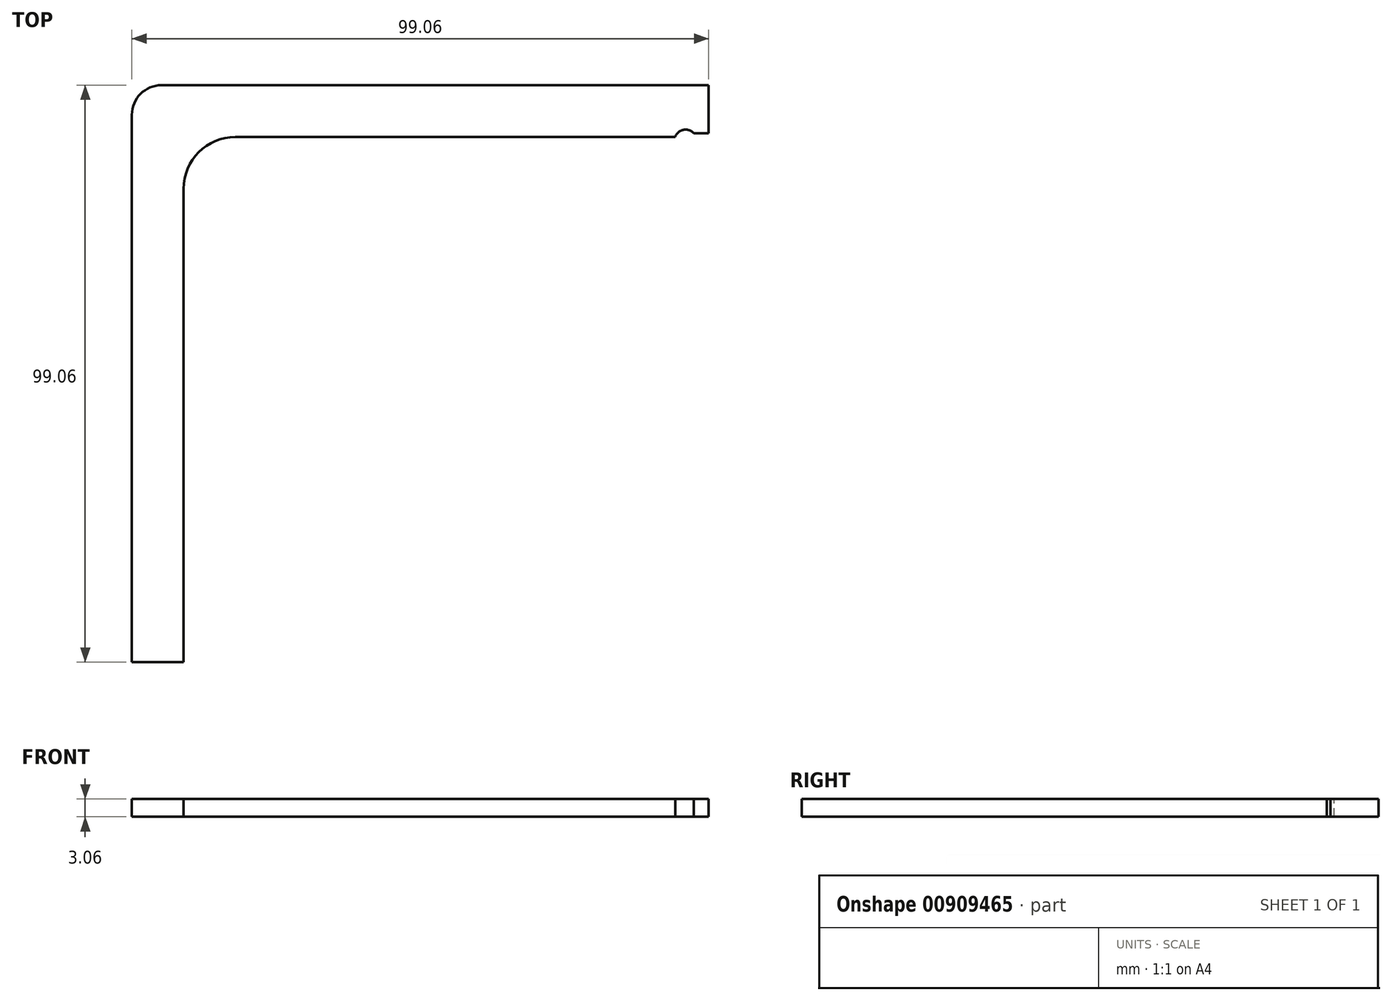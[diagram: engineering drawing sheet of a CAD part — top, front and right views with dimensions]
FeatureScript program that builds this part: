
annotation { "Feature Type Name" : "Feature", "Feature Type Description" : "" }
export const myFeature = defineFeature(function(context is Context, id is Id, definition is map)
    precondition{}
    {
        {
            var Q0;
            Q0=qCreatedBy(makeId("Top.planeOp"),FACE);
            var sketch = newSketch(context, id + "F0", { "sketchPlane" : qUnion([Q0])});
            skLineSegment(sketch, "E0.bottom", {"start": v(99.06, -99.06) * mm, "end": v(-99.06, -99.06) * mm});
            skLineSegment(sketch, "E0.top", {"start": v(99.06, 99.06) * mm, "end": v(-99.06, 99.06) * mm});
            skLineSegment(sketch, "E0.left", {"start": v(99.06, -99.06) * mm, "end": v(99.06, 99.06) * mm});
            skLineSegment(sketch, "E0.right", {"start": v(-99.06, -99.06) * mm, "end": v(-99.06, 99.06) * mm});
            skPoint(sketch, "E0.middle", {"position": v(0, 0) * mm});
            skLineSegment(sketch, "E1.bottom", {"start": v(86.36, 86.36) * mm, "end": v(-86.36, 86.36) * mm});
            skLineSegment(sketch, "E1.top", {"start": v(86.36, -86.36) * mm, "end": v(-86.36, -86.36) * mm});
            skLineSegment(sketch, "E1.left", {"start": v(86.36, 86.36) * mm, "end": v(86.36, -86.36) * mm});
            skLineSegment(sketch, "E1.right", {"start": v(-86.36, 86.36) * mm, "end": v(-86.36, -86.36) * mm});
            skSolve(sketch);
        }
        {
            var Q0;
            Q0=qSketchRegion(id+"F0",true);
            extrude(context, id + "F1", {"entities" : qUnion([Q0]), "depth" : (0.12 + 0.25 + (5.38 / 2)) * mm, "offsetDistance" : 25.4 * mm});
        }
        {
            var Q0;
            Q0=qCreatedBy(makeId("Top.planeOp"),FACE);
            cPlane(context, id + "F2", {"entities" : qUnion([Q0]), "cplaneType" : CPlaneType.OFFSET, "offset" : 6.35 * mm, "width" : 152.4 * mm, "height" : 152.4 * mm});
        }
        {
            var Q0;
            Q0=qCreatedBy(id+"F2.planeOp",FACE);
            var sketch = newSketch(context, id + "F3", { "sketchPlane" : qUnion([Q0])});
            skLineSegment(sketch, "E2.bottom", {"start": v(99.06, 99.06) * mm, "end": v(-99.06, 99.06) * mm});
            skLineSegment(sketch, "E2.top", {"start": v(99.06, -99.06) * mm, "end": v(-99.06, -99.06) * mm});
            skLineSegment(sketch, "E2.left", {"start": v(99.06, 99.06) * mm, "end": v(99.06, -99.06) * mm});
            skLineSegment(sketch, "E2.right", {"start": v(-99.06, 99.06) * mm, "end": v(-99.06, -99.06) * mm});
            skPoint(sketch, "E2.middle", {"position": v(0, 0) * mm});
            skLineSegment(sketch, "E3.bottom", {"start": v(92.71, 92.71) * mm, "end": v(-92.71, 92.71) * mm});
            skLineSegment(sketch, "E3.top", {"start": v(92.71, -92.71) * mm, "end": v(-92.71, -92.71) * mm});
            skLineSegment(sketch, "E3.left", {"start": v(92.71, 92.71) * mm, "end": v(92.71, -92.71) * mm});
            skLineSegment(sketch, "E3.right", {"start": v(-92.71, 92.71) * mm, "end": v(-92.71, -92.71) * mm});
            skSolve(sketch);
        }
        {
            var Q0;
            Q0=qSketchRegion(id+"F3",true);
            extrude(context, id + "F4", {"entities" : qUnion([Q0]), "operationType" : NewBodyOperationType.REMOVE, "endBound" : BoundingType.THROUGH_ALL, "depth" : 25.4 * mm, "offsetDistance" : 25.4 * mm});
        }
        {
            var Q0;
            Q0=makeQuery(id+"F1.opExtrude","SWEPT_EDGE",EDGE,{"disambiguationData":[OSD([sQuery(id+"F0.wireOp",EDGE,"E0.top"),sQuery(id+"F0.wireOp",EDGE,"E0.left")])]});
            var Q1;
            Q1=makeQuery(id+"F1.opExtrude","SWEPT_EDGE",EDGE,{"disambiguationData":[OSD([sQuery(id+"F0.wireOp",EDGE,"E0.top"),sQuery(id+"F0.wireOp",EDGE,"E0.right")])]});
            var Q2;
            Q2=makeQuery(id+"F4.boolean.opBoolean","COPY",EDGE,{"derivedFrom":makeQuery(id+"F4.opExtrude","SWEPT_EDGE",EDGE,{"disambiguationData":[OSD([sQuery(id+"F3.wireOp",EDGE,"E3.bottom"),sQuery(id+"F3.wireOp",EDGE,"E3.right")])]})});
            var Q3;
            Q3=makeQuery(id+"F4.boolean.opBoolean","COPY",EDGE,{"derivedFrom":makeQuery(id+"F4.opExtrude","SWEPT_EDGE",EDGE,{"disambiguationData":[OSD([sQuery(id+"F3.wireOp",EDGE,"E3.bottom"),sQuery(id+"F3.wireOp",EDGE,"E3.left")])]})});
            var Q4;
            Q4=makeQuery(id+"F1.opExtrude","SWEPT_EDGE",EDGE,{"disambiguationData":[OSD([sQuery(id+"F0.wireOp",EDGE,"E0.bottom"),sQuery(id+"F0.wireOp",EDGE,"E0.right")])]});
            var Q5;
            Q5=makeQuery(id+"F4.boolean.opBoolean","COPY",EDGE,{"derivedFrom":makeQuery(id+"F4.opExtrude","SWEPT_EDGE",EDGE,{"disambiguationData":[OSD([sQuery(id+"F3.wireOp",EDGE,"E3.top"),sQuery(id+"F3.wireOp",EDGE,"E3.right")])]})});
            var Q6;
            Q6=makeQuery(id+"F1.opExtrude","SWEPT_EDGE",EDGE,{"disambiguationData":[OSD([sQuery(id+"F0.wireOp",EDGE,"E0.bottom"),sQuery(id+"F0.wireOp",EDGE,"E0.left")])]});
            var Q7;
            Q7=makeQuery(id+"F4.boolean.opBoolean","COPY",EDGE,{"derivedFrom":makeQuery(id+"F4.opExtrude","SWEPT_EDGE",EDGE,{"disambiguationData":[OSD([sQuery(id+"F3.wireOp",EDGE,"E3.top"),sQuery(id+"F3.wireOp",EDGE,"E3.left")])]})});
            var Q8;
            Q8=makeQuery(id+"F1.opExtrude","SWEPT_EDGE",EDGE,{"disambiguationData":[OSD([sQuery(id+"F0.wireOp",EDGE,"E1.top"),sQuery(id+"F0.wireOp",EDGE,"E1.right")])]});
            var Q9;
            Q9=makeQuery(id+"F1.opExtrude","SWEPT_EDGE",EDGE,{"disambiguationData":[OSD([sQuery(id+"F0.wireOp",EDGE,"E1.top"),sQuery(id+"F0.wireOp",EDGE,"E1.left")])]});
            var Q10;
            Q10=makeQuery(id+"F1.opExtrude","SWEPT_EDGE",EDGE,{"disambiguationData":[OSD([sQuery(id+"F0.wireOp",EDGE,"E1.bottom"),sQuery(id+"F0.wireOp",EDGE,"E1.right")])]});
            var Q11;
            Q11=makeQuery(id+"F1.opExtrude","SWEPT_EDGE",EDGE,{"disambiguationData":[OSD([sQuery(id+"F0.wireOp",EDGE,"E1.bottom"),sQuery(id+"F0.wireOp",EDGE,"E1.left")])]});
            fillet(context, id + "F5", {"entities" : qUnion([Q0, Q1, Q2, Q3, Q4, Q5, Q6, Q7, Q8, Q9, Q10, Q11]), "radius" : 5.08 * mm, "tangentPropagation" : true, "allowEdgeOverflow" : false});
        }
        {
            var Q0;
            Q0=qCreatedBy(makeId("Front.planeOp"),FACE);
            var sketch = newSketch(context, id + "F6", { "sketchPlane" : qUnion([Q0])});
            skLineSegment(sketch, "E4.bottom", {"start": v(-137.33, -39.02) * mm, "end": v(163.38, -39.02) * mm});
            skLineSegment(sketch, "E4.top", {"start": v(-137.33, 123.29) * mm, "end": v(163.38, 123.29) * mm});
            skLineSegment(sketch, "E4.left", {"start": v(-137.33, -39.02) * mm, "end": v(-137.33, 123.29) * mm});
            skLineSegment(sketch, "E4.right", {"start": v(163.38, -39.02) * mm, "end": v(163.38, 123.29) * mm});
            skSolve(sketch);
        }
        {
            var Q0;
            Q0=qSketchRegion(id+"F6",true);
            extrude(context, id + "F7", {"entities" : qUnion([Q0]), "operationType" : NewBodyOperationType.REMOVE, "endBound" : BoundingType.THROUGH_ALL, "depth" : 25.4 * mm, "offsetDistance" : 25.4 * mm});
        }
        {
            var Q0;
            Q0=qCreatedBy(makeId("Right.planeOp"),FACE);
            var sketch = newSketch(context, id + "F8", { "sketchPlane" : qUnion([Q0])});
            skLineSegment(sketch, "E5.bottom", {"start": v(-40.9, -45.65) * mm, "end": v(117.43, -45.65) * mm});
            skLineSegment(sketch, "E5.top", {"start": v(-40.9, 78.34) * mm, "end": v(117.43, 78.34) * mm});
            skLineSegment(sketch, "E5.left", {"start": v(-40.9, -45.65) * mm, "end": v(-40.9, 78.34) * mm});
            skLineSegment(sketch, "E5.right", {"start": v(117.43, -45.65) * mm, "end": v(117.43, 78.34) * mm});
            skSolve(sketch);
        }
        {
            var Q0;
            Q0=qSketchRegion(id+"F8",true);
            extrude(context, id + "F9", {"entities" : qUnion([Q0]), "operationType" : NewBodyOperationType.REMOVE, "endBound" : BoundingType.THROUGH_ALL, "depth" : 25.4 * mm, "offsetDistance" : 25.4 * mm});
        }
        {
            var Q0;
            Q0=makeQuery(id+"F1.opExtrude","CAP_FACE",FACE,{"disambiguationData":[OSD([sQuery(id+"F0.wireOp",EDGE,"E0.bottom"),sQuery(id+"F0.wireOp",EDGE,"E0.top"),sQuery(id+"F0.wireOp",EDGE,"E0.left"),sQuery(id+"F0.wireOp",EDGE,"E0.right"),sQuery(id+"F0.wireOp",EDGE,"E1.bottom"),sQuery(id+"F0.wireOp",EDGE,"E1.top"),sQuery(id+"F0.wireOp",EDGE,"E1.left"),sQuery(id+"F0.wireOp",EDGE,"E1.right")])],"isStart":false});
            var sketch = newSketch(context, id + "F10", { "sketchPlane" : qUnion([Q0])});
            skArc(sketch, "E6", {"start": v(-2.54, 90.8) * mm, "mid": v(-5.86, 89.53) * mm, "end": v(-2.54, 88.27) * mm});
            skLineSegment(sketch, "E7", {"start": v(-2.54, 90.8) * mm, "end": v(0, 90.8) * mm});
            skLineSegment(sketch, "E8", {"start": v(0, 90.8) * mm, "end": v(0, 88.27) * mm});
            skLineSegment(sketch, "E9", {"start": v(0, 88.27) * mm, "end": v(-2.54, 88.27) * mm});
            skLineSegment(sketch, "E10", {"start": v(0, 89.54) * mm, "end": v(-3.96, 89.54) * mm, "construction": true});
            skSolve(sketch);
        }
        {
            var Q0;
            Q0 = qSketchRegion(id + "F10", true);
            extrude(context, id + "F11", {"entities" : qUnion([Q0]), "operationType" : NewBodyOperationType.REMOVE, "endBound" : BoundingType.THROUGH_ALL, "oppositeDirection" : true, "depth" : 25.4 * mm, "offsetDistance" : 25.4 * mm});
        }
        {
            var Q0;
            Q0=makeQuery(id+"F1.opExtrude","CAP_FACE",FACE,{"disambiguationData":[OSD([sQuery(id+"F0.wireOp",EDGE,"E0.bottom"),sQuery(id+"F0.wireOp",EDGE,"E0.top"),sQuery(id+"F0.wireOp",EDGE,"E0.left"),sQuery(id+"F0.wireOp",EDGE,"E0.right"),sQuery(id+"F0.wireOp",EDGE,"E1.bottom"),sQuery(id+"F0.wireOp",EDGE,"E1.top"),sQuery(id+"F0.wireOp",EDGE,"E1.left"),sQuery(id+"F0.wireOp",EDGE,"E1.right")])],"isStart":false});
            var sketch = newSketch(context, id + "F12", { "sketchPlane" : qUnion([Q0])});
            skArc(sketch, "E11", {"start": v(-90.8, -2.54) * mm, "mid": v(-89.53, -5.86) * mm, "end": v(-88.27, -2.54) * mm, "construction": true});
            skLineSegment(sketch, "E12", {"start": v(-88.27, -2.54) * mm, "end": v(-88.27, 0) * mm, "construction": true});
            skLineSegment(sketch, "E13", {"start": v(-88.27, 0) * mm, "end": v(-90.8, 0) * mm, "construction": true});
            skLineSegment(sketch, "E14", {"start": v(-90.8, 0) * mm, "end": v(-90.8, -2.54) * mm, "construction": true});
            skLineSegment(sketch, "E15", {"start": v(0, 90.8) * mm, "end": v(0, 88.27) * mm, "construction": true});
            skLineSegment(sketch, "E16", {"start": v(-89.53, 0) * mm, "end": v(-89.53, 7.06) * mm, "construction": true});
            skLineSegment(sketch, "E17.0", {"start": v(-88.5, -2.65) * mm, "end": v(-88.5, -0.23) * mm, "construction": true});
            skArc(sketch, "E17.1", {"start": v(-90.58, -2.65) * mm, "mid": v(-89.53, -5.64) * mm, "end": v(-88.5, -2.65) * mm, "construction": true});
            skLineSegment(sketch, "E17.2", {"start": v(-90.58, -0.23) * mm, "end": v(-90.58, -2.65) * mm, "construction": true});
            skLineSegment(sketch, "E17.3", {"start": v(-88.5, -0.23) * mm, "end": v(-90.58, -0.23) * mm, "construction": true});
            skLineSegment(sketch, "E18", {"start": v(-90.58, -2.65) * mm, "end": v(-90.58, 0) * mm});
            skLineSegment(sketch, "E19", {"start": v(-90.58, 0) * mm, "end": v(-88.5, 0) * mm});
            skLineSegment(sketch, "E20", {"start": v(-88.5, 0) * mm, "end": v(-88.5, -2.65) * mm});
            skArc(sketch, "E21", {"start": v(-90.58, -2.65) * mm, "mid": v(-89.53, -5.64) * mm, "end": v(-88.5, -2.65) * mm});
            skSolve(sketch);
        }
        {
            var Q0;
            Q0 = qSketchRegion(id + "F12", true);
            var Q1;
            Q1=makeQuery(id+"F1.opExtrude","CAP_FACE",FACE,{"disambiguationData":[OSD([sQuery(id+"F0.wireOp",EDGE,"E0.bottom"),sQuery(id+"F0.wireOp",EDGE,"E0.top"),sQuery(id+"F0.wireOp",EDGE,"E0.left"),sQuery(id+"F0.wireOp",EDGE,"E0.right"),sQuery(id+"F0.wireOp",EDGE,"E1.bottom"),sQuery(id+"F0.wireOp",EDGE,"E1.top"),sQuery(id+"F0.wireOp",EDGE,"E1.left"),sQuery(id+"F0.wireOp",EDGE,"E1.right")])],"isStart":true});
            extrude(context, id + "F13", {"entities" : qUnion([Q0]), "operationType" : NewBodyOperationType.ADD, "endBound" : BoundingType.UP_TO_SURFACE, "oppositeDirection" : true, "depth" : 25.4 * mm, "endBoundEntityFace" : qUnion([Q1]), "offsetDistance" : 25.4 * mm});
        }
        {
            var Q0;
            Q0=makeQuery(id+"F13.boolean.opBoolean","MERGE",FACE,{"derivedFrom":[makeQuery(id+"F1.opExtrude","CAP_FACE",FACE,{"disambiguationData":[OSD([sQuery(id+"F0.wireOp",EDGE,"E0.bottom"),sQuery(id+"F0.wireOp",EDGE,"E0.top"),sQuery(id+"F0.wireOp",EDGE,"E0.left"),sQuery(id+"F0.wireOp",EDGE,"E0.right"),sQuery(id+"F0.wireOp",EDGE,"E1.bottom"),sQuery(id+"F0.wireOp",EDGE,"E1.top"),sQuery(id+"F0.wireOp",EDGE,"E1.left"),sQuery(id+"F0.wireOp",EDGE,"E1.right")])],"isStart":false}),makeQuery(id+"F13.opExtrude","CAP_FACE",FACE,{"disambiguationData":[OSD([sQuery(id+"F12.wireOp",EDGE,"E18"),sQuery(id+"F12.wireOp",EDGE,"E19"),sQuery(id+"F12.wireOp",EDGE,"E20"),sQuery(id+"F12.wireOp",EDGE,"E21")])],"isStart":true})]});
            var sketch = newSketch(context, id + "F14", { "sketchPlane" : qUnion([Q0])});
            skLineSegment(sketch, "E22", {"start": v(0, 86.36) * mm, "end": v(-81.28, 86.36) * mm});
            skLineSegment(sketch, "E23", {"start": v(-86.36, 81.28) * mm, "end": v(-86.36, 0) * mm});
            skLineSegment(sketch, "E24", {"start": v(-85.25, -6.28) * mm, "end": v(-95.33, -6.28) * mm});
            skLineSegment(sketch, "E25", {"start": v(-95.33, -6.28) * mm, "end": v(-90.58, 0) * mm});
            skLineSegment(sketch, "E26", {"start": v(-90.58, 0) * mm, "end": v(-90.17, 0) * mm});
            skLineSegment(sketch, "E27", {"start": v(-90.17, 0) * mm, "end": v(-90.17, 81.28) * mm});
            skLineSegment(sketch, "E28", {"start": v(-86.36, 0) * mm, "end": v(-85.25, -6.28) * mm});
            skArc(sketch, "E29", {"start": v(-81.28, 90.17) * mm, "mid": v(-87.57, 87.57) * mm, "end": v(-90.17, 81.28) * mm});
            skArc(sketch, "E30", {"start": v(-81.28, 86.36) * mm, "mid": v(-84.87, 84.87) * mm, "end": v(-86.36, 81.28) * mm});
            skLineSegment(sketch, "E31", {"start": v(-81.28, 90.17) * mm, "end": v(-5.76, 90.17) * mm});
            skLineSegment(sketch, "E32", {"start": v(0, 86.36) * mm, "end": v(0, 88.27) * mm});
            skLineSegment(sketch, "E33", {"start": v(0, 88.27) * mm, "end": v(-2.54, 88.27) * mm});
            skArc(sketch, "E34", {"start": v(-5.76, 90.17) * mm, "mid": v(-4.93, 87.9) * mm, "end": v(-2.54, 88.27) * mm});
            skSolve(sketch);
        }
        {
            var Q0;
            Q0 = qSketchRegion(id + "F14", true);
            extrude(context, id + "F15", {"entities" : qUnion([Q0]), "operationType" : NewBodyOperationType.REMOVE, "oppositeDirection" : true, "depth" : 12.7 * mm, "offsetDistance" : 25.4 * mm});
        }
    });
